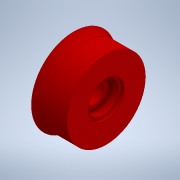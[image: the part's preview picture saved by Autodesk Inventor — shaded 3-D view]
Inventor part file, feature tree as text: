
AUTODESK INVENTOR PART (.ipt)
format: ipt  version: 2020 (Build 240168000, 168)  size: 272,896 bytes
history: native  units: mm
features: extrude x5, sketch x5, other x3, fillet x2, projected_geometry x1
ambient origin geometry x8: Origin, YZ Plane, XZ Plane, XY Plane, X Axis, Y Axis, Z Axis, Center Point
bodies: Solid1 (feature_tree)
feature tree (16):
  other  "WeaponMountBasePlateV1.ipt"
  extrude  "Extrusion1"  Depth=10.0mm
  extrude  "Extrusion2"  TaperAngle=0.0deg  [1 undecoded]
  extrude  "Extrusion3"  Depth=0.75mm
  fillet  "Fillet1"  [1 undecoded]
  fillet  "Fillet2"  Radius=7.3mm
  extrude  "Extrusion4"  TaperAngle=0.0deg  [1 undecoded]
  extrude  "Extrusion5"  Depth=5.0mm
  other  "Solid1::WeaponMountBasePlateV1.ipt"
  other  "TaggingFeature1"
  sketch  "Sketch2"  dims[d0=10.0mm d2=18.43mm]
  sketch  "Sketch3"  dims[d3=10.0mm d4=0.0mm]
  sketch  "Sketch4"  dims[d5=8.43mm d6=0.75mm d7=0.0mm d8=7.3mm]
  projected_geometry  "Projected Loop1"
  sketch  "Sketch5"  dims[d9=1.9mm d10=0.0mm]
  sketch  "Sketch6"  dims[d11=1.5mm d12=5.0mm d13=4.5mm d14=5.0mm d15=0.0mm d16=10.0mm d17=0.0mm]
note: 3 required parameter values undecoded (feature->parameter linkage not recoverable at this tier; creation-order binding heuristic only, values carry confidence <= 0.55)
